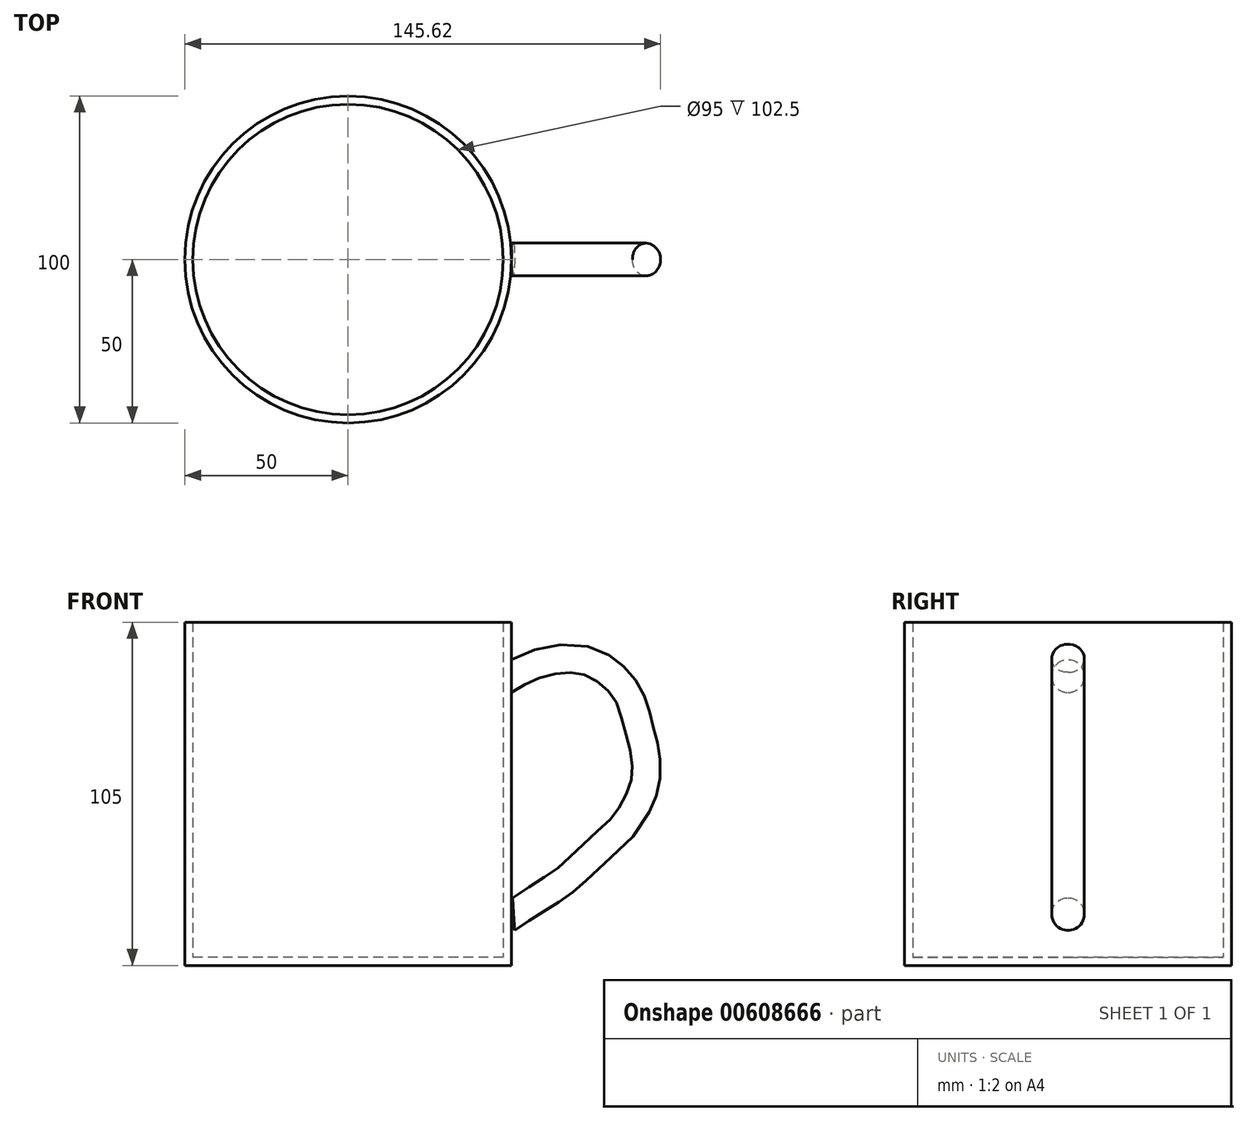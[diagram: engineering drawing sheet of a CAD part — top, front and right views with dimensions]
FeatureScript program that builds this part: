
annotation { "Feature Type Name" : "Feature", "Feature Type Description" : "" }
export const myFeature = defineFeature(function(context is Context, id is Id, definition is map)
    precondition{}
    {
        {
            var Q0;
            Q0=qCreatedBy(makeId("Top.planeOp"),FACE);
            var sketch = newSketch(context, id + "F0", { "sketchPlane" : qUnion([Q0])});
            skCircle(sketch, "E0", {"center": v(0, 0) * mm, "radius": 50 * mm});
            skSolve(sketch);
        }
        {
            var Q0;
            Q0 = qSketchRegion(id + "F0", true);
            extrude(context, id + "F1", {"entities" : qUnion([Q0]), "depth" : 105 * mm, "offsetDistance" : 25.4 * mm});
        }
        {
            var Q0;
            Q0=qCreatedBy(makeId("Right.planeOp"),FACE);
            cPlane(context, id + "F2", {"entities" : qUnion([Q0]), "cplaneType" : CPlaneType.OFFSET, "offset" : 50 * mm, "width" : 152.4 * mm, "height" : 152.4 * mm});
        }
        {
            var Q0;
            Q0=qCreatedBy(makeId("Front.planeOp"),FACE);
            var sketch = newSketch(context, id + "F3", { "sketchPlane" : qUnion([Q0])});
            skFitSpline(sketch, "E1", {"points": [v(50.3, 87.72) * mm, v(56.88, 91) * mm, v(66.09, 92.98) * mm, v(73.98, 91.88) * mm, v(80.55, 87.72) * mm, v(85.38, 81.36) * mm, v(87.79, 73.91) * mm, v(89.76, 66.02) * mm, v(90.2, 57.47) * mm, v(88, 50.46) * mm, v(83.84, 43.66) * mm, v(78.58, 38.4) * mm, v(71.57, 31.83) * mm, v(65, 26.13) * mm, v(58.42, 21.74) * mm, v(50.3, 16.48) * mm], "startDerivative": vector(97.72, 56.01) * mm, "endDerivative": vector(-115.05, -75.34) * mm});
            skSolve(sketch);
        }
        {
            var Q0;
            Q0=qCreatedBy(id+"F2.planeOp",FACE);
            var sketch = newSketch(context, id + "F4", { "sketchPlane" : qUnion([Q0])});
            skCircle(sketch, "E2", {"center": v(0, 88.5) * mm, "radius": 5 * mm});
            skCircle(sketch, "E3", {"center": v(0, 16.74) * mm, "radius": 5 * mm});
            skSolve(sketch);
        }
        {
            var Q0;
            Q0=makeQuery(id+"F4.imprint","IMPRINT",FACE,{"disambiguationData":[TD([[makeQuery(id+"F4.imprint","IMPRINT",EDGE,{"derivedFrom":sQuery(id+"F4.wireOp",EDGE,"E2")}),1.0]])]});
            var Q1;
            Q1=sQuery(id+"F3.wireOp",EDGE,"E1");
            sweep(context, id + "F5", {"operationType" : NewBodyOperationType.ADD, "profiles" : qUnion([Q0]), "path" : qUnion([Q1])});
        }
        {
            var Q0;
            Q0=makeQuery(id+"F1.opExtrude","CAP_FACE",FACE,{"disambiguationData":[OSD([sQuery(id+"F0.wireOp",EDGE,"E0")])],"isStart":false});
            shell(context, id + "F6", {"entities" : qUnion([Q0]), "thickness" : 2.5 * mm});
        }
    });
